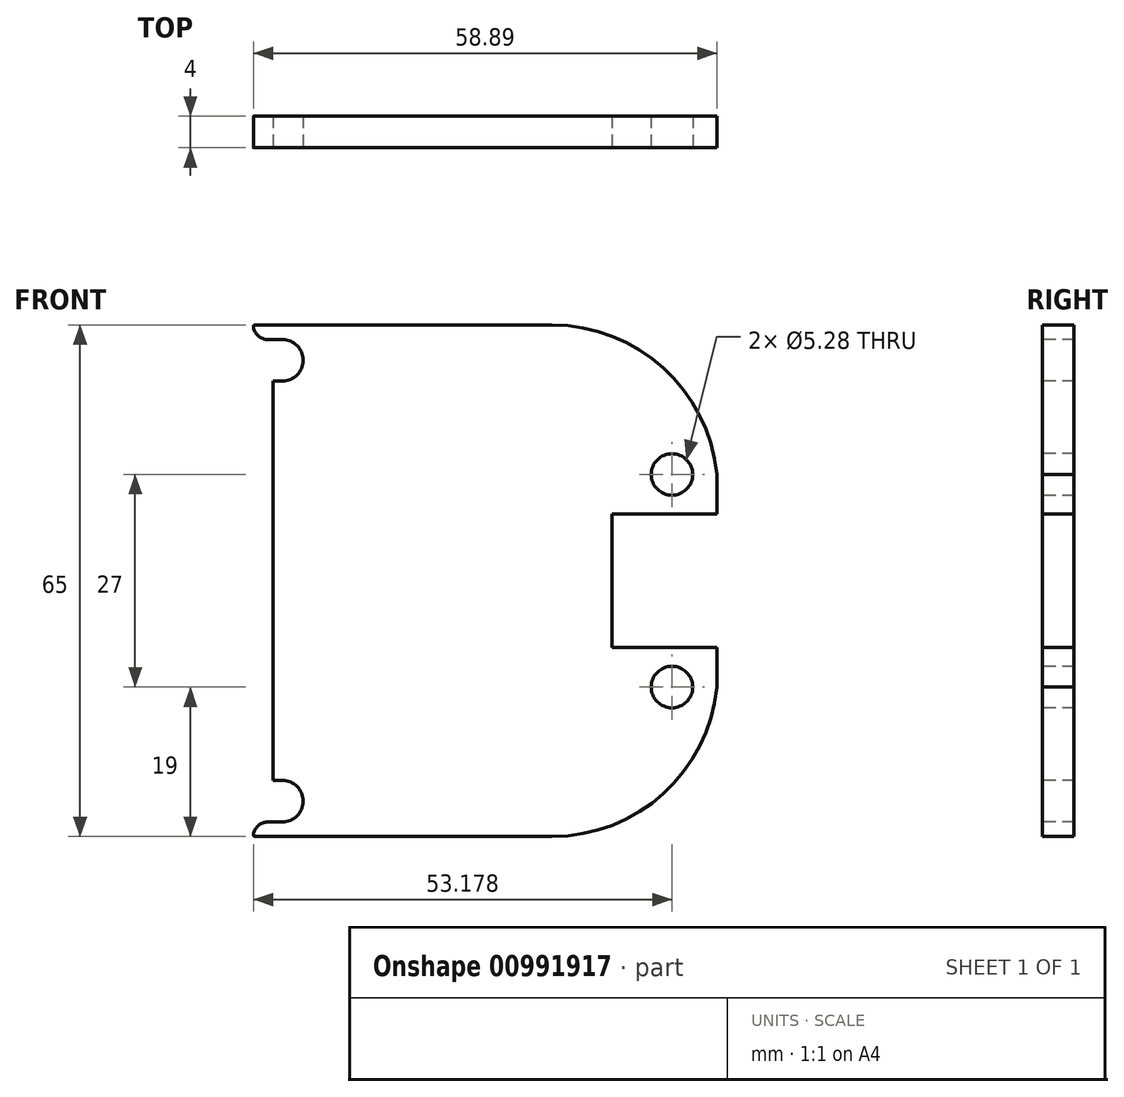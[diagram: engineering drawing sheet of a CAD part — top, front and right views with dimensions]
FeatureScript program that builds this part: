
annotation { "Feature Type Name" : "Feature", "Feature Type Description" : "" }
export const myFeature = defineFeature(function(context is Context, id is Id, definition is map)
    precondition{}
    {
        {
            var Q0;
            Q0=qCreatedBy(makeId("Front.planeOp"),FACE);
            var sketch = newSketch(context, id + "F0", { "sketchPlane" : qUnion([Q0])});
            skLineSegment(sketch, "E0.bottom", {"start": v(34.26, 37.43) * mm, "end": v(-34.26, 37.43) * mm});
            skLineSegment(sketch, "E0.top", {"start": v(34.26, -37.43) * mm, "end": v(-34.26, -37.43) * mm});
            skLineSegment(sketch, "E0.left", {"start": v(34.26, 37.43) * mm, "end": v(34.26, -37.43) * mm});
            skLineSegment(sketch, "E0.right", {"start": v(-34.26, 37.43) * mm, "end": v(-34.26, -37.43) * mm});
            skPoint(sketch, "E0.middle", {"position": v(0, 0) * mm});
            skSolve(sketch);
        }
        {
            var Q0;
            Q0=makeQuery(id+"F0.imprint","IMPRINT",FACE,{"disambiguationData":[TD([[makeQuery(id+"F0.imprint","IMPRINT",EDGE,{"derivedFrom":sQuery(id+"F0.wireOp",EDGE,"E0.bottom")}),1.0]])]});
            extrude(context, id + "F1", {"entities" : qUnion([Q0]), "depth" : 4 * mm});
        }
        {
            var Q0;
            Q0=makeQuery(id+"F1.opExtrude","CAP_FACE",FACE,{"disambiguationData":[OSD([sQuery(id+"F0.wireOp",EDGE,"E0.bottom"),sQuery(id+"F0.wireOp",EDGE,"E0.top"),sQuery(id+"F0.wireOp",EDGE,"E0.left"),sQuery(id+"F0.wireOp",EDGE,"E0.right")])],"isStart":false});
            var sketch = newSketch(context, id + "F2", { "sketchPlane" : qUnion([Q0])});
            skCircle(sketch, "E1", {"center": v(-34.26, 28) * mm, "radius": 2.64 * mm});
            skCircle(sketch, "E2", {"center": v(15.24, 13.5) * mm, "radius": 2.64 * mm});
            skLineSegment(sketch, "E3", {"start": v(-34.26, 0) * mm, "end": v(34.26, 0) * mm, "construction": true});
            skCircle(sketch, "E4.MirrorC", {"center": v(-34.26, -28) * mm, "radius": 2.64 * mm});
            skCircle(sketch, "E5.MirrorC", {"center": v(15.24, -13.5) * mm, "radius": 2.64 * mm});
            skLineSegment(sketch, "E6.bottom", {"start": v(7.64, 8.5) * mm, "end": v(20.95, 8.5) * mm});
            skLineSegment(sketch, "E7", {"start": v(-34.26, 32.5) * mm, "end": v(0, 32.5) * mm});
            skArc(sketch, "E8", {"start": v(0, 32.5) * mm, "mid": v(14.14, 27.04) * mm, "end": v(20.95, 13.5) * mm});
            skPoint(sketch, "E8.endSnap0", {"position": v(20.95, 8.5) * mm});
            skLineSegment(sketch, "E9", {"start": v(20.95, 13.5) * mm, "end": v(20.95, 8.5) * mm});
            skLineSegment(sketch, "E10", {"start": v(-34.26, 32.5) * mm, "end": v(-34.26, 37.43) * mm});
            skLineSegment(sketch, "E11", {"start": v(-34.26, 37.43) * mm, "end": v(34.26, 37.43) * mm});
            skLineSegment(sketch, "E12", {"start": v(34.26, 37.43) * mm, "end": v(34.26, 8.5) * mm});
            skLineSegment(sketch, "E13", {"start": v(7.64, 8.5) * mm, "end": v(7.64, 0) * mm});
            skLineSegment(sketch, "E14", {"start": v(7.64, 0) * mm, "end": v(34.26, 0) * mm});
            skLineSegment(sketch, "E15", {"start": v(34.26, 8.5) * mm, "end": v(34.26, 0) * mm});
            skLineSegment(sketch, "E16.MirrorCS", {"start": v(7.64, -8.5) * mm, "end": v(7.64, 0) * mm});
            skLineSegment(sketch, "E17.MirrorCS", {"start": v(7.64, -8.5) * mm, "end": v(20.95, -8.5) * mm});
            skLineSegment(sketch, "E18.MirrorCS", {"start": v(20.95, -13.5) * mm, "end": v(20.95, -8.5) * mm});
            skArc(sketch, "E19.MirrorCS", {"start": v(0, -32.5) * mm, "mid": v(14.14, -27.04) * mm, "end": v(20.95, -13.5) * mm});
            skLineSegment(sketch, "E20.MirrorCS", {"start": v(-34.26, -32.5) * mm, "end": v(0, -32.5) * mm});
            skLineSegment(sketch, "E21.MirrorCS", {"start": v(-34.26, -32.5) * mm, "end": v(-34.26, -37.43) * mm});
            skLineSegment(sketch, "E22.MirrorCS", {"start": v(-34.26, -37.43) * mm, "end": v(34.26, -37.43) * mm});
            skLineSegment(sketch, "E23.MirrorCS", {"start": v(34.26, -37.43) * mm, "end": v(34.26, -8.5) * mm});
            skLineSegment(sketch, "E24.MirrorCS", {"start": v(34.26, -8.5) * mm, "end": v(34.26, 0) * mm});
            skSolve(sketch);
        }
        {
            var Q0;
            Q0=qSketchRegion(id+"F2",true);
            extrude(context, id + "F3", {"entities" : qUnion([Q0]), "operationType" : NewBodyOperationType.REMOVE, "endBound" : BoundingType.THROUGH_ALL, "oppositeDirection" : true, "depth" : 25.4 * mm});
        }
        {
            var Q0;
            Q0=makeQuery(id+"F1.opExtrude","CAP_FACE",FACE,{"disambiguationData":[OSD([sQuery(id+"F0.wireOp",EDGE,"E0.bottom"),sQuery(id+"F0.wireOp",EDGE,"E0.top"),sQuery(id+"F0.wireOp",EDGE,"E0.left"),sQuery(id+"F0.wireOp",EDGE,"E0.right")])],"isStart":false});
            var sketch = newSketch(context, id + "F4", { "sketchPlane" : qUnion([Q0])});
            skLineSegment(sketch, "E25.bottom", {"start": v(-34.26, 25.36) * mm, "end": v(-35.46, 25.36) * mm});
            skLineSegment(sketch, "E25.top", {"start": v(-34.26, -25.36) * mm, "end": v(-35.46, -25.36) * mm});
            skLineSegment(sketch, "E25.left", {"start": v(-34.26, 25.36) * mm, "end": v(-34.26, -25.36) * mm});
            skLineSegment(sketch, "E25.right", {"start": v(-35.46, 25.36) * mm, "end": v(-35.46, -25.36) * mm});
            skLineSegment(sketch, "E26", {"start": v(-34.26, 30.64) * mm, "end": v(-36.06, 30.64) * mm});
            skArc(sketch, "E27", {"start": v(-36.06, 30.64) * mm, "mid": v(-37.4, 31.18) * mm, "end": v(-37.97, 32.5) * mm});
            skLineSegment(sketch, "E28", {"start": v(-37.97, 32.5) * mm, "end": v(-34.26, 32.5) * mm});
            skLineSegment(sketch, "E29", {"start": v(-35.46, 0) * mm, "end": v(0, 0) * mm, "construction": true});
            skArc(sketch, "E30.MirrorCS", {"start": v(-36.06, -30.64) * mm, "mid": v(-37.4, -31.18) * mm, "end": v(-37.97, -32.5) * mm});
            skLineSegment(sketch, "E31.MirrorCS", {"start": v(-34.26, -30.64) * mm, "end": v(-36.06, -30.64) * mm});
            skLineSegment(sketch, "E32.MirrorCS", {"start": v(-37.97, -32.5) * mm, "end": v(-34.26, -32.5) * mm});
            skSolve(sketch);
        }
        {
            var Q0;
            Q0=makeQuery(id+"F4.imprint","IMPRINT",FACE,{"disambiguationData":[TD([[makeQuery(id+"F4.imprint","IMPRINT",EDGE,{"derivedFrom":sQuery(id+"F4.wireOp",EDGE,"E30.MirrorCS")}),1.0]])]});
            var Q1;
            Q1=makeQuery(id+"F4.imprint","IMPRINT",FACE,{"disambiguationData":[TD([[makeQuery(id+"F4.imprint","IMPRINT",EDGE,{"derivedFrom":sQuery(id+"F4.wireOp",EDGE,"E25.bottom")}),1.0]])]});
            var Q2;
            Q2=makeQuery(id+"F4.imprint","IMPRINT",FACE,{"disambiguationData":[TD([[makeQuery(id+"F4.imprint","IMPRINT",EDGE,{"derivedFrom":sQuery(id+"F4.wireOp",EDGE,"E26")}),-1.0]])]});
            var Q3;
            Q3=makeQuery(id+"F1.opExtrude","CAP_FACE",FACE,{"disambiguationData":[OSD([sQuery(id+"F0.wireOp",EDGE,"E0.bottom"),sQuery(id+"F0.wireOp",EDGE,"E0.top"),sQuery(id+"F0.wireOp",EDGE,"E0.left"),sQuery(id+"F0.wireOp",EDGE,"E0.right")])],"isStart":true});
            extrude(context, id + "F5", {"entities" : qUnion([Q0, Q1, Q2]), "operationType" : NewBodyOperationType.ADD, "endBound" : BoundingType.UP_TO_SURFACE, "oppositeDirection" : true, "endBoundEntityFace" : qUnion([Q3]), "depth" : 25.4 * mm});
        }
        {
            var Q0;
            Q0=makeQuery(id+"F5.opExtrude","SWEPT_EDGE",EDGE,{"disambiguationData":[OSD([sQuery(id+"F4.wireOp",EDGE,"E30.MirrorCS"),sQuery(id+"F4.wireOp",EDGE,"E32.MirrorCS")])]});
            var Q1;
            Q1=makeQuery(id+"F5.opExtrude","SWEPT_EDGE",EDGE,{"disambiguationData":[OSD([sQuery(id+"F4.wireOp",EDGE,"E27"),sQuery(id+"F4.wireOp",EDGE,"E28")])]});
            fillet(context, id + "F6", {"entities" : qUnion([Q0, Q1]), "radius" : 0.25 * mm, "allowEdgeOverflow" : false});
        }
    });
